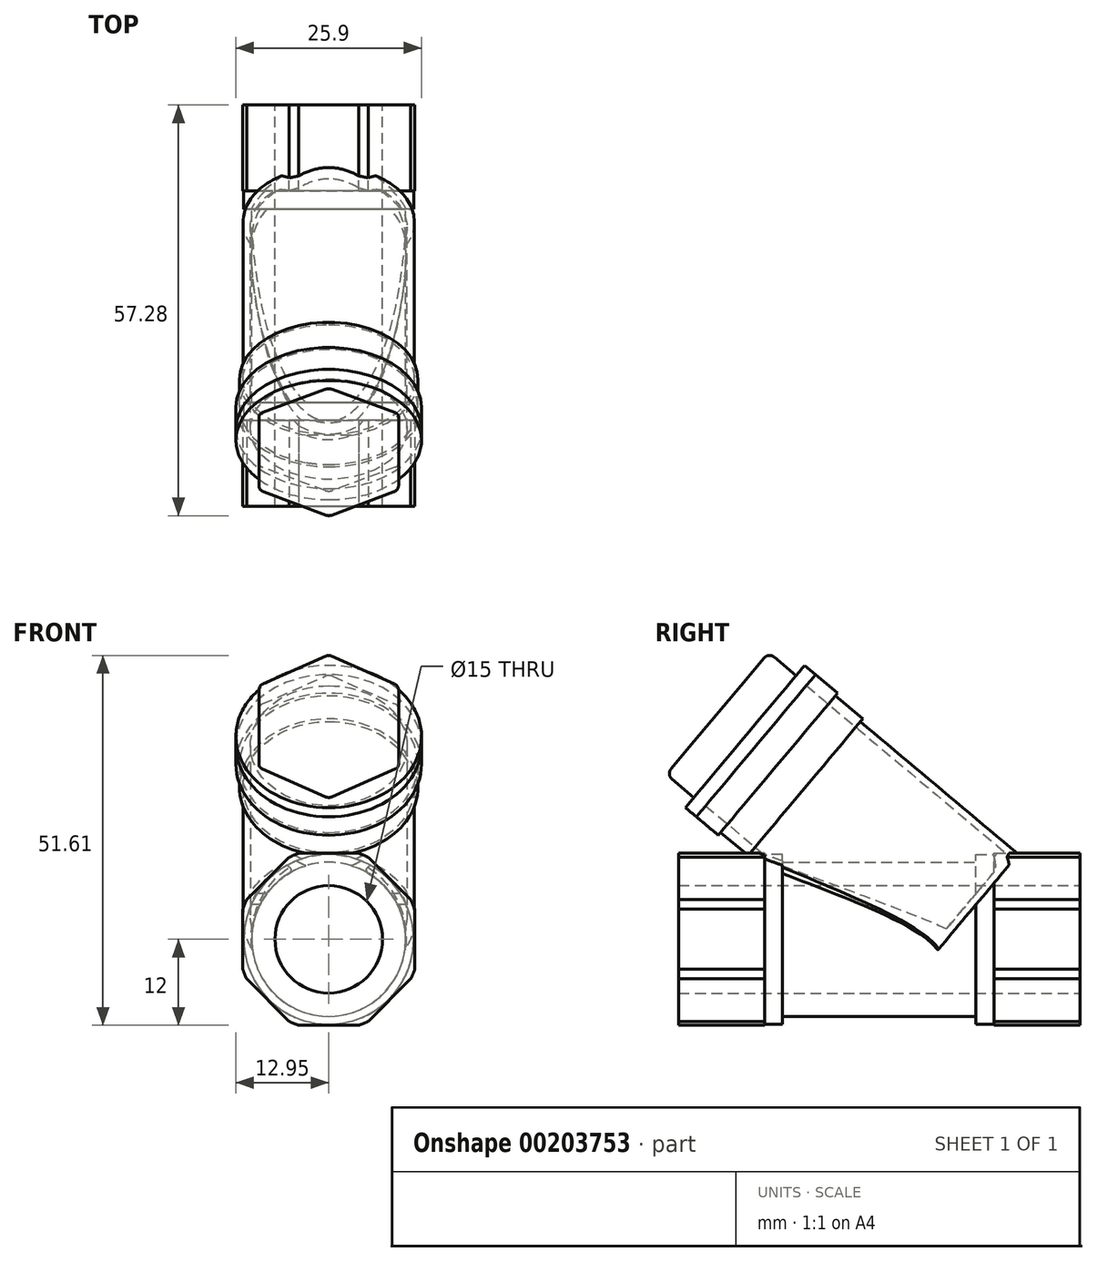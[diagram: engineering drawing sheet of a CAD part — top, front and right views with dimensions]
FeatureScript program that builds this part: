
annotation { "Feature Type Name" : "Feature", "Feature Type Description" : "" }
export const myFeature = defineFeature(function(context is Context, id is Id, definition is map)
    precondition{}
    {
        {
            var Q0;
            Q0=qCreatedBy(makeId("Front.planeOp"),FACE);
            var sketch = newSketch(context, id + "F0", { "sketchPlane" : qUnion([Q0])});
            skCircle(sketch, "E0", {"center": v(0, 0) * mm, "radius": 12.7 * mm});
            skCircle(sketch, "E1.cCircle", {"center": v(0, 0) * mm, "radius": 12 * mm, "construction": true});
            skLineSegment(sketch, "E1.0", {"start": v(-4.97, 12) * mm, "end": v(4.97, 12) * mm});
            skLineSegment(sketch, "E1.1", {"start": v(4.97, 12) * mm, "end": v(12, 4.97) * mm});
            skLineSegment(sketch, "E1.2", {"start": v(12, 4.97) * mm, "end": v(12, -4.97) * mm});
            skLineSegment(sketch, "E1.3", {"start": v(12, -4.97) * mm, "end": v(4.97, -12) * mm});
            skLineSegment(sketch, "E1.4", {"start": v(4.97, -12) * mm, "end": v(-4.97, -12) * mm});
            skLineSegment(sketch, "E1.5", {"start": v(-4.97, -12) * mm, "end": v(-12, -4.97) * mm});
            skLineSegment(sketch, "E1.6", {"start": v(-12, -4.97) * mm, "end": v(-12, 4.97) * mm});
            skLineSegment(sketch, "E1.7", {"start": v(-12, 4.97) * mm, "end": v(-4.97, 12) * mm});
            skPoint(sketch, "E1.0.midPoint", {"position": v(0, 12) * mm});
            skCircle(sketch, "E2", {"center": v(0, 0) * mm, "radius": 7.5 * mm});
            skSolve(sketch);
        }
        {
            var Q0;
            Q0=makeQuery(id+"F0.imprint","IMPRINT",FACE,{"disambiguationData":[TD([[makeQuery(id+"F0.imprint","IMPRINT",EDGE,{"derivedFrom":sQuery(id+"F0.wireOp",EDGE,"E2")}),-1.0]])]});
            extrude(context, id + "F1", {"entities" : qUnion([Q0]), "depth" : 12 * mm});
        }
        {
            var Q0;
            Q0=makeQuery(id+"F1.opExtrude","CAP_FACE",FACE,{"disambiguationData":[OSD([sQuery(id+"F0.wireOp",EDGE,"E0"),sQuery(id+"F0.wireOp",EDGE,"E1.0"),sQuery(id+"F0.wireOp",EDGE,"E1.1"),sQuery(id+"F0.wireOp",EDGE,"E1.2"),sQuery(id+"F0.wireOp",EDGE,"E1.3"),sQuery(id+"F0.wireOp",EDGE,"E1.4"),sQuery(id+"F0.wireOp",EDGE,"E1.5"),sQuery(id+"F0.wireOp",EDGE,"E1.6"),sQuery(id+"F0.wireOp",EDGE,"E1.7"),sQuery(id+"F0.wireOp",EDGE,"E2")])],"isStart":false});
            var sketch = newSketch(context, id + "F2", { "sketchPlane" : qUnion([Q0])});
            skCircle(sketch, "E3", {"center": v(0, 0) * mm, "radius": 11.85 * mm});
            skCircle(sketch, "E4", {"center": v(0, 0) * mm, "radius": 7.5 * mm});
            skSolve(sketch);
        }
        {
            var Q0;
            Q0 = qSketchRegion(id + "F2", true);
            extrude(context, id + "F3", {"entities" : qUnion([Q0]), "operationType" : NewBodyOperationType.ADD, "depth" : 2.5 * mm});
        }
        {
            var Q0;
            Q0=makeQuery(id+"F3.opExtrude","CAP_FACE",FACE,{"disambiguationData":[OSD([sQuery(id+"F2.wireOp",EDGE,"E3"),sQuery(id+"F2.wireOp",EDGE,"E4")])],"isStart":false});
            var sketch = newSketch(context, id + "F4", { "sketchPlane" : qUnion([Q0])});
            skCircle(sketch, "E5", {"center": v(0, 0) * mm, "radius": 7.5 * mm});
            skCircle(sketch, "E6", {"center": v(0, 0) * mm, "radius": 10.75 * mm});
            skSolve(sketch);
        }
        {
            var Q0;
            Q0 = qSketchRegion(id + "F4", true);
            extrude(context, id + "F5", {"entities" : qUnion([Q0]), "operationType" : NewBodyOperationType.ADD, "depth" : 13.5 * mm});
        }
        {
            var Q0;
            Q0=makeQuery(id+"F5.opExtrude","CAP_FACE",FACE,{"disambiguationData":[OSD([sQuery(id+"F4.wireOp",EDGE,"E5"),sQuery(id+"F4.wireOp",EDGE,"E6")])],"isStart":false});
            cPlane(context, id + "F6", {"entities" : qUnion([Q0]), "cplaneType" : CPlaneType.OFFSET, "offset" : 0 * mm, "width" : 150 * mm, "height" : 150 * mm});
        }
        {
            var Q0;
            Q0=makeQuery(id+"F1.opExtrude","SWEPT_BODY",BODY,{"disambiguationData":[OSD([sQuery(id+"F0.wireOp",EDGE,"E0"),sQuery(id+"F0.wireOp",EDGE,"E1.0"),sQuery(id+"F0.wireOp",EDGE,"E1.1"),sQuery(id+"F0.wireOp",EDGE,"E1.2"),sQuery(id+"F0.wireOp",EDGE,"E1.3"),sQuery(id+"F0.wireOp",EDGE,"E1.4"),sQuery(id+"F0.wireOp",EDGE,"E1.5"),sQuery(id+"F0.wireOp",EDGE,"E1.6"),sQuery(id+"F0.wireOp",EDGE,"E1.7"),sQuery(id+"F0.wireOp",EDGE,"E2")])]});
            var Q1;
            Q1=qCreatedBy(id+"F6.planeOp",FACE);
            mirror(context, id + "F7", {"operationType" : NewBodyOperationType.ADD, "entities" : qUnion([Q0]), "mirrorPlane" : qUnion([Q1])});
        }
        {
            var Q0;
            Q0=qCreatedBy(makeId("Right.planeOp"),FACE);
            var sketch = newSketch(context, id + "F8", { "sketchPlane" : qUnion([Q0])});
            skLineSegment(sketch, "E7", {"start": v(-30, 0) * mm, "end": v(-45.32, 12.86) * mm});
            skLineSegment(sketch, "E8", {"start": v(-30, 0) * mm, "end": v(-39.2, 0) * mm, "construction": true});
            skLineSegment(sketch, "E9", {"start": v(-30, 0) * mm, "end": v(-28, 0) * mm, "construction": true});
            skLineSegment(sketch, "E10", {"start": v(-13, 0) * mm, "end": v(-31.04, 15.14) * mm, "construction": true});
            skLineSegment(sketch, "E11", {"start": v(-30, 0) * mm, "end": v(-24.04, -5) * mm});
            skLineSegment(sketch, "E12", {"start": v(-24.04, -5) * mm, "end": v(-40.97, -5) * mm, "construction": true});
            skLineSegment(sketch, "E13", {"start": v(-24.04, -5) * mm, "end": v(-17.02, 3.37) * mm});
            skLineSegment(sketch, "E14", {"start": v(-17.02, 3.37) * mm, "end": v(-17.48, 3.76) * mm});
            skLineSegment(sketch, "E15", {"start": v(-44.8, 13.48) * mm, "end": v(-45.32, 12.86) * mm});
            skLineSegment(sketch, "E16", {"start": v(-45.32, 12.86) * mm, "end": v(-45.98, 12.08) * mm});
            skLineSegment(sketch, "E17", {"start": v(-45.98, 12.08) * mm, "end": v(-23.95, -6.4) * mm});
            skLineSegment(sketch, "E18", {"start": v(-23.95, -6.4) * mm, "end": v(-16.27, 2.74) * mm});
            skLineSegment(sketch, "E19", {"start": v(-16.27, 2.74) * mm, "end": v(-17.02, 3.37) * mm});
            skSolve(sketch);
        }
        {
            var Q0;
            Q0=makeQuery(id+"F8.imprint","IMPRINT",FACE,{"disambiguationData":[TD([[makeQuery(id+"F8.imprint","IMPRINT",EDGE,{"derivedFrom":sQuery(id+"F8.wireOp",EDGE,"E7")}),1.0]])]});
            var Q1;
            Q1=sQuery(id+"F8.wireOp",EDGE,"E11");
            var Q2;
            Q2=sQuery(id+"F8.wireOp",EDGE,"E7");
            var Q3;
            Q3=sQuery(id+"F8.wireOp",EDGE,"E10");
            revolve(context, id + "F9", {"entities" : qUnion([Q0]), "surfaceEntities" : qUnion([Q1, Q2]), "axis" : qUnion([Q3]), "revolveType" : RevolveType.FULL});
        }
        {
            var Q0;
            Q0=makeQuery(id+"F1.opExtrude","SWEPT_BODY",BODY,{"disambiguationData":[OSD([sQuery(id+"F0.wireOp",EDGE,"E0"),sQuery(id+"F0.wireOp",EDGE,"E1.0"),sQuery(id+"F0.wireOp",EDGE,"E1.1"),sQuery(id+"F0.wireOp",EDGE,"E1.2"),sQuery(id+"F0.wireOp",EDGE,"E1.3"),sQuery(id+"F0.wireOp",EDGE,"E1.4"),sQuery(id+"F0.wireOp",EDGE,"E1.5"),sQuery(id+"F0.wireOp",EDGE,"E1.6"),sQuery(id+"F0.wireOp",EDGE,"E1.7"),sQuery(id+"F0.wireOp",EDGE,"E2")])]});
            var Q1;
            Q1=makeQuery(id+"F9.opRevolve","SWEPT_BODY",BODY,{"disambiguationData":[OSD([sQuery(id+"F8.wireOp",EDGE,"E7"),sQuery(id+"F8.wireOp",EDGE,"E11"),sQuery(id+"F8.wireOp",EDGE,"E13"),sQuery(id+"F8.wireOp",EDGE,"E16"),sQuery(id+"F8.wireOp",EDGE,"E17"),sQuery(id+"F8.wireOp",EDGE,"E18"),sQuery(id+"F8.wireOp",EDGE,"E19")])]});
            booleanBodies(context, id + "F10", {"operationType" : BooleanOperationType.UNION, "tools" : qUnion([Q0, Q1])});
        }
        {
            var Q0;
            {var subQ0=makeQuery(id+"F5.opExtrude","SWEPT_FACE",FACE,{"disambiguationData":[OSD([sQuery(id+"F4.wireOp",EDGE,"E6")])]});Q0=makeQuery(id+"F10.opBoolean","INTERSECT",EDGE,{"disambiguationData":[OD(0.0)],"derivedFrom":[makeQuery(id+"F7.boolean.opBoolean","MERGE",FACE,{"derivedFrom":[subQ0,makeQuery(id+"F7.opPattern","COPY",FACE,{"derivedFrom":subQ0,"instanceName":"1"})]}),makeQuery(id+"F9.opRevolve","SWEPT_FACE",FACE,{"disambiguationData":[OSD([sQuery(id+"F8.wireOp",EDGE,"E17")])]})]});}
            var Q1;
            {var subQ0=makeQuery(id+"F5.opExtrude","SWEPT_FACE",FACE,{"disambiguationData":[OSD([sQuery(id+"F4.wireOp",EDGE,"E6")])]});Q1=makeQuery(id+"F10.opBoolean","INTERSECT",EDGE,{"disambiguationData":[OD(1.0)],"derivedFrom":[makeQuery(id+"F7.boolean.opBoolean","MERGE",FACE,{"derivedFrom":[subQ0,makeQuery(id+"F7.opPattern","COPY",FACE,{"derivedFrom":subQ0,"instanceName":"1"})]}),makeQuery(id+"F9.opRevolve","SWEPT_FACE",FACE,{"disambiguationData":[OSD([sQuery(id+"F8.wireOp",EDGE,"E17")])]})]});}
            fillet(context, id + "F11", {"entities" : qUnion([Q0, Q1]), "radius" : 0.5 * mm, "tangentPropagation" : true, "allowEdgeOverflow" : false});
        }
        {
            var Q0;
            Q0=makeQuery(id+"F9.opRevolve","SWEPT_FACE",FACE,{"disambiguationData":[OSD([sQuery(id+"F8.wireOp",EDGE,"E16")])]});
            var sketch = newSketch(context, id + "F12", { "sketchPlane" : qUnion([Q0])});
            skCircle(sketch, "E20", {"center": v(0, -8.36) * mm, "radius": 10.45 * mm});
            skCircle(sketch, "E21", {"center": v(0, -8.36) * mm, "radius": 12.45 * mm});
            skSolve(sketch);
        }
        {
            var Q0;
            Q0=makeQuery(id+"F9.opRevolve","SWEPT_FACE",FACE,{"disambiguationData":[OSD([sQuery(id+"F8.wireOp",EDGE,"E16")])]});
            var Q1;
            Q1=makeQuery(id+"F12.imprint","IMPRINT",FACE,{"disambiguationData":[TD([[makeQuery(id+"F12.imprint","IMPRINT",EDGE,{"derivedFrom":sQuery(id+"F12.wireOp",EDGE,"E21")}),1.0]])]});
            var Q2;
            Q2=makeQuery(id+"F2S3Vq0ay0OpAwi_1.opExtrude","CAP_FACE",FACE,{"disambiguationData":[OSD([sQuery(id+"FXccv6XCxqiLoGx_1.wireOp",EDGE,"W4jMlvvA-8WaT-1PAN-S9XS-eXb3TYS7VGb8"),sQuery(id+"FXccv6XCxqiLoGx_1.wireOp",EDGE,"zpnE0Raa-npXJ-0FG6-Y6QP-CpcaHiAozYsv")])],"isStart":false});
            extrude(context, id + "F13", {"entities" : qUnion([Q0, Q1, Q2]), "operationType" : NewBodyOperationType.ADD, "depth" : 5 * mm});
        }
        {
            var Q0;
            {var subQ0=sQuery(id+"F8.wireOp",EDGE,"E16");Q0=makeQuery(id+"F13.boolean.opBoolean","MERGE",FACE,{"derivedFrom":[makeQuery(id+"F13.opExtrude","CAP_FACE",FACE,{"disambiguationData":[OSD([subQ0])],"isStart":false}),makeQuery(id+"F13.opExtrude","CAP_FACE",FACE,{"disambiguationData":[OSD([subQ0,sQuery(id+"F8.wireOp",EDGE,"E17"),sQuery(id+"F12.wireOp",EDGE,"E21")])],"isStart":false})]});}
            var sketch = newSketch(context, id + "F14", { "sketchPlane" : qUnion([Q0])});
            skCircle(sketch, "E22", {"center": v(0, -8.36) * mm, "radius": 10.45 * mm});
            skCircle(sketch, "E23", {"center": v(0, -8.36) * mm, "radius": 12.95 * mm});
            skSolve(sketch);
        }
        {
            var Q0;
            Q0=makeQuery(id+"F14.imprint","IMPRINT",FACE,{"disambiguationData":[TD([[makeQuery(id+"F14.imprint","IMPRINT",EDGE,{"derivedFrom":sQuery(id+"F14.wireOp",EDGE,"E23")}),1.0]])]});
            var Q1;
            Q1=makeQuery(id+"F13.opExtrude","CAP_FACE",FACE,{"disambiguationData":[OSD([sQuery(id+"FXccv6XCxqiLoGx_1.wireOp",EDGE,"W4jMlvvA-8WaT-1PAN-S9XS-eXb3TYS7VGb8"),sQuery(id+"FXccv6XCxqiLoGx_1.wireOp",EDGE,"zpnE0Raa-npXJ-0FG6-Y6QP-CpcaHiAozYsv")])],"isStart":false});
            var Q2;
            {var subQ0=sQuery(id+"F8.wireOp",EDGE,"E16");Q2=makeQuery(id+"F13.boolean.opBoolean","MERGE",FACE,{"derivedFrom":[makeQuery(id+"F13.opExtrude","CAP_FACE",FACE,{"disambiguationData":[OSD([subQ0])],"isStart":false}),makeQuery(id+"F13.opExtrude","CAP_FACE",FACE,{"disambiguationData":[OSD([subQ0,sQuery(id+"F8.wireOp",EDGE,"E17"),sQuery(id+"F12.wireOp",EDGE,"E21")])],"isStart":false})]});}
            extrude(context, id + "F15", {"entities" : qUnion([Q0, Q1, Q2]), "operationType" : NewBodyOperationType.ADD, "depth" : 4 * mm});
        }
        {
            var Q0;
            Q0=makeQuery(id+"F7.opPattern","COPY",FACE,{"derivedFrom":makeQuery(id+"F1.opExtrude","CAP_FACE",FACE,{"disambiguationData":[OSD([sQuery(id+"F0.wireOp",EDGE,"E0"),sQuery(id+"F0.wireOp",EDGE,"E1.0"),sQuery(id+"F0.wireOp",EDGE,"E1.1"),sQuery(id+"F0.wireOp",EDGE,"E1.2"),sQuery(id+"F0.wireOp",EDGE,"E1.3"),sQuery(id+"F0.wireOp",EDGE,"E1.4"),sQuery(id+"F0.wireOp",EDGE,"E1.5"),sQuery(id+"F0.wireOp",EDGE,"E1.6"),sQuery(id+"F0.wireOp",EDGE,"E1.7"),sQuery(id+"F0.wireOp",EDGE,"E2")])],"isStart":true}),"instanceName":"1"});
            var sketch = newSketch(context, id + "F16", { "sketchPlane" : qUnion([Q0])});
            skCircle(sketch, "E24", {"center": v(0, 0) * mm, "radius": 7.5 * mm});
            skSolve(sketch);
        }
        {
            var Q0;
            Q0 = qSketchRegion(id + "F16", true);
            extrude(context, id + "F17", {"entities" : qUnion([Q0]), "operationType" : NewBodyOperationType.REMOVE, "oppositeDirection" : true, "depth" : 59 * mm});
        }
        {
            var Q0;
            {var subQ0=sQuery(id+"F12.wireOp",EDGE,"E21");Q0=makeQuery(id+"F15.boolean.opBoolean","MERGE",FACE,{"derivedFrom":[makeQuery(id+"F15.opExtrude","CAP_FACE",FACE,{"disambiguationData":[OSD([sQuery(id+"F8.wireOp",EDGE,"E16"),sQuery(id+"F8.wireOp",EDGE,"E17"),subQ0])],"isStart":false}),makeQuery(id+"F15.opExtrude","CAP_FACE",FACE,{"disambiguationData":[OSD([subQ0,sQuery(id+"F14.wireOp",EDGE,"E23")])],"isStart":false})]});}
            var sketch = newSketch(context, id + "F18", { "sketchPlane" : qUnion([Q0])});
            skCircle(sketch, "E25", {"center": v(0, -8.36) * mm, "radius": 12.95 * mm});
            skSolve(sketch);
        }
        {
            var Q0;
            Q0 = qSketchRegion(id + "F18", true);
            extrude(context, id + "F19", {"entities" : qUnion([Q0]), "depth" : 2 * mm});
        }
        {
            var Q0;
            Q0=makeQuery(id+"F19.opExtrude","CAP_FACE",FACE,{"disambiguationData":[OSD([sQuery(id+"F18.wireOp",EDGE,"E25")])],"isStart":false});
            var sketch = newSketch(context, id + "F20", { "sketchPlane" : qUnion([Q0])});
            skCircle(sketch, "E26.cCircle", {"center": v(0, -8.36) * mm, "radius": 9.75 * mm, "construction": true});
            skLineSegment(sketch, "E26.0", {"start": v(0, 2.9) * mm, "end": v(9.75, -2.73) * mm});
            skLineSegment(sketch, "E26.1", {"start": v(9.75, -2.73) * mm, "end": v(9.75, -13.99) * mm});
            skLineSegment(sketch, "E26.2", {"start": v(9.75, -13.99) * mm, "end": v(0, -19.61) * mm});
            skLineSegment(sketch, "E26.3", {"start": v(0, -19.61) * mm, "end": v(-9.75, -13.99) * mm});
            skLineSegment(sketch, "E26.4", {"start": v(-9.75, -13.99) * mm, "end": v(-9.75, -2.73) * mm});
            skLineSegment(sketch, "E26.5", {"start": v(-9.75, -2.73) * mm, "end": v(0, 2.9) * mm});
            skPoint(sketch, "E26.0.midPoint", {"position": v(4.87, 0.09) * mm});
            skSolve(sketch);
        }
        {
            var Q0;
            Q0=makeQuery(id+"F20.imprint","IMPRINT",FACE,{"disambiguationData":[TD([[makeQuery(id+"F20.imprint","IMPRINT",EDGE,{"derivedFrom":sQuery(id+"F20.wireOp",EDGE,"E26.0")}),-1.0]])]});
            extrude(context, id + "F21", {"entities" : qUnion([Q0]), "operationType" : NewBodyOperationType.ADD, "depth" : 5 * mm});
        }
        {
            var Q0;
            Q0=makeQuery(id+"F21.opExtrude","SWEPT_EDGE",EDGE,{"disambiguationData":[OSD([sQuery(id+"F20.wireOp",EDGE,"E26.0"),sQuery(id+"F20.wireOp",EDGE,"E26.5")])]});
            var Q1;
            Q1=makeQuery(id+"F21.opExtrude","SWEPT_EDGE",EDGE,{"disambiguationData":[OSD([sQuery(id+"F20.wireOp",EDGE,"E26.0"),sQuery(id+"F20.wireOp",EDGE,"E26.1")])]});
            var Q2;
            Q2=makeQuery(id+"F21.opExtrude","SWEPT_EDGE",EDGE,{"disambiguationData":[OSD([sQuery(id+"F20.wireOp",EDGE,"E26.1"),sQuery(id+"F20.wireOp",EDGE,"E26.2")])]});
            var Q3;
            Q3=makeQuery(id+"F21.opExtrude","SWEPT_EDGE",EDGE,{"disambiguationData":[OSD([sQuery(id+"F20.wireOp",EDGE,"E26.2"),sQuery(id+"F20.wireOp",EDGE,"E26.3")])]});
            var Q4;
            Q4=makeQuery(id+"F21.opExtrude","SWEPT_EDGE",EDGE,{"disambiguationData":[OSD([sQuery(id+"F20.wireOp",EDGE,"E26.3"),sQuery(id+"F20.wireOp",EDGE,"E26.4")])]});
            var Q5;
            Q5=makeQuery(id+"F21.opExtrude","SWEPT_EDGE",EDGE,{"disambiguationData":[OSD([sQuery(id+"F20.wireOp",EDGE,"E26.4"),sQuery(id+"F20.wireOp",EDGE,"E26.5")])]});
            var Q6;
            Q6=makeQuery(id+"F21.opExtrude","CAP_FACE",FACE,{"disambiguationData":[OSD([sQuery(id+"F20.wireOp",EDGE,"E26.0"),sQuery(id+"F20.wireOp",EDGE,"E26.1"),sQuery(id+"F20.wireOp",EDGE,"E26.2"),sQuery(id+"F20.wireOp",EDGE,"E26.3"),sQuery(id+"F20.wireOp",EDGE,"E26.4"),sQuery(id+"F20.wireOp",EDGE,"E26.5")])],"isStart":false});
            fillet(context, id + "F22", {"entities" : qUnion([Q0, Q1, Q2, Q3, Q4, Q5, Q6]), "radius" : 1 * mm, "tangentPropagation" : true, "allowEdgeOverflow" : false});
        }
    });
